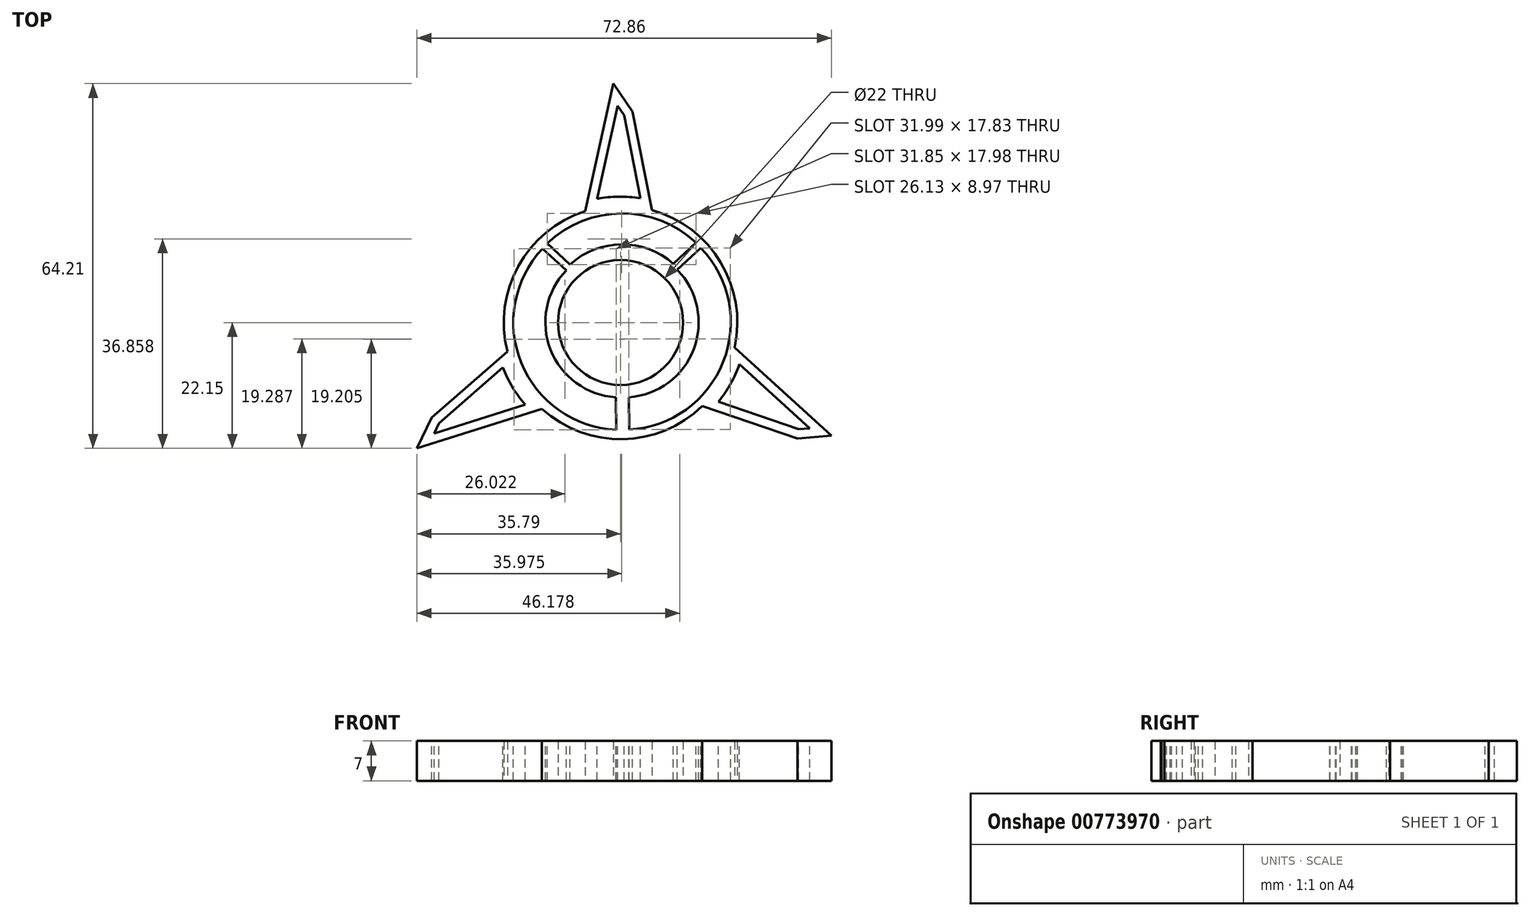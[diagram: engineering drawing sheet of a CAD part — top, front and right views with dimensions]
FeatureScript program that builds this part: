
annotation { "Feature Type Name" : "Feature", "Feature Type Description" : "" }
export const myFeature = defineFeature(function(context is Context, id is Id, definition is map)
    precondition{}
    {
        {
            var Q0;
            Q0=qCreatedBy(makeId("Top.planeOp"),FACE);
            var sketch = newSketch(context, id + "F0", { "sketchPlane" : qUnion([Q0])});
            skCircle(sketch, "E0", {"center": v(0, 0) * mm, "radius": 11 * mm});
            skCircle(sketch, "E1", {"center": v(0, 0) * mm, "radius": 20.54 * mm});
            skLineSegment(sketch, "E2", {"start": v(-6.23, 19.57) * mm, "end": v(0, 47.93) * mm});
            skLineSegment(sketch, "E3", {"start": v(0, 47.93) * mm, "end": v(5.52, 19.79) * mm});
            skLineSegment(sketch, "E4.1.0", {"start": v(-41.5, -23.96) * mm, "end": v(-19.9, -5.11) * mm});
            skLineSegment(sketch, "E4.1.1", {"start": v(-13.83, -15.18) * mm, "end": v(-41.5, -23.96) * mm});
            skLineSegment(sketch, "E4.2.0", {"start": v(41.5, -23.96) * mm, "end": v(14.38, -14.67) * mm});
            skLineSegment(sketch, "E4.2.1", {"start": v(20.07, -4.39) * mm, "end": v(41.5, -23.96) * mm});
            skSolve(sketch);
        }
        {
            var Q0;
            Q0=qSketchRegion(id+"F0",true);
            extrude(context, id + "F1", {"entities" : qUnion([Q0]), "depth" : 7 * mm, "offsetDistance" : 25 * mm});
        }
        {
            var Q0;
            Q0=makeQuery(id+"F1.opExtrude","CAP_FACE",FACE,{"disambiguationData":[OSD([sQuery(id+"F0.wireOp",EDGE,"E0"),sQuery(id+"F0.wireOp",EDGE,"E1"),sQuery(id+"F0.wireOp",EDGE,"E2"),sQuery(id+"F0.wireOp",EDGE,"E3"),sQuery(id+"F0.wireOp",EDGE,"E4.1.0"),sQuery(id+"F0.wireOp",EDGE,"E4.1.1"),sQuery(id+"F0.wireOp",EDGE,"E4.2.0"),sQuery(id+"F0.wireOp",EDGE,"E4.2.1")])],"isStart":false});
            var sketch = newSketch(context, id + "F2", { "sketchPlane" : qUnion([Q0])});
            skLineSegment(sketch, "E5", {"start": v(-13.74, 12.98) * mm, "end": v(-9.55, 9.18) * mm});
            skLineSegment(sketch, "E6", {"start": v(0, 47.93) * mm, "end": v(0.37, -20.54) * mm, "construction": true});
            skLineSegment(sketch, "E7.MirrorCS", {"start": v(14.12, 13.13) * mm, "end": v(9.98, 9.28) * mm});
            skLineSegment(sketch, "E8", {"start": v(-0.8, -13.16) * mm, "end": v(-0.78, -18.87) * mm});
            skLineSegment(sketch, "E9.MirrorCS", {"start": v(1.47, -13.15) * mm, "end": v(1.5, -18.86) * mm});
            skArc(sketch, "E10", {"start": v(-9.55, 9.18) * mm, "mid": v(-12.3, -4.78) * mm, "end": v(-0.8, -13.16) * mm});
            skArc(sketch, "E11", {"start": v(-13.74, 12.98) * mm, "mid": v(-17.46, -7.1) * mm, "end": v(-0.78, -18.87) * mm});
            skLineSegment(sketch, "E12", {"start": v(-12.88, 13.93) * mm, "end": v(-8.89, 10.22) * mm});
            skArc(sketch, "E13.MirrorCS", {"start": v(14.12, 13.13) * mm, "mid": v(18.06, -6.9) * mm, "end": v(1.5, -18.86) * mm});
            skArc(sketch, "E14.MirrorCS", {"start": v(9.98, 9.28) * mm, "mid": v(12.88, -4.65) * mm, "end": v(1.47, -13.15) * mm});
            skLineSegment(sketch, "E15.MirrorCS", {"start": v(13.25, 14.07) * mm, "end": v(9.3, 10.32) * mm});
            skArc(sketch, "E16", {"start": v(9.3, 10.32) * mm, "mid": v(0.19, 13.75) * mm, "end": v(-8.89, 10.22) * mm});
            skArc(sketch, "E17", {"start": v(13.25, 14.07) * mm, "mid": v(0.16, 19.2) * mm, "end": v(-12.88, 13.93) * mm});
            skSolve(sketch);
        }
        {
            var Q0;
            Q0=qSketchRegion(id+"F2",true);
            extrude(context, id + "F3", {"entities" : qUnion([Q0]), "operationType" : NewBodyOperationType.REMOVE, "oppositeDirection" : true, "depth" : 25 * mm, "offsetDistance" : 25 * mm});
        }
        {
            var Q0;
            Q0=makeQuery(id+"F1.opExtrude","SWEPT_EDGE",EDGE,{"disambiguationData":[OSD([sQuery(id+"F0.wireOp",EDGE,"E4.1.0"),sQuery(id+"F0.wireOp",EDGE,"E4.1.1")])]});
            var Q1;
            Q1=makeQuery(id+"F1.opExtrude","SWEPT_EDGE",EDGE,{"disambiguationData":[OSD([sQuery(id+"F0.wireOp",EDGE,"E2"),sQuery(id+"F0.wireOp",EDGE,"E3")])]});
            var Q2;
            Q2=makeQuery(id+"F1.opExtrude","SWEPT_EDGE",EDGE,{"disambiguationData":[OSD([sQuery(id+"F0.wireOp",EDGE,"E4.2.0"),sQuery(id+"F0.wireOp",EDGE,"E4.2.1")])]});
            chamfer(context, id + "F4", {"entities" : qUnion([Q0, Q1, Q2]), "chamferType" : ChamferType.TWO_OFFSETS, "width1" : 6 * mm, "oppositeDirection" : false, "width2" : 11 * mm, "tangentPropagation" : true});
        }
        {
            var Q0;
            Q0=makeQuery(id+"F1.opExtrude","CAP_FACE",FACE,{"disambiguationData":[OSD([sQuery(id+"F0.wireOp",EDGE,"E0"),sQuery(id+"F0.wireOp",EDGE,"E1"),sQuery(id+"F0.wireOp",EDGE,"E2"),sQuery(id+"F0.wireOp",EDGE,"E3"),sQuery(id+"F0.wireOp",EDGE,"E4.1.0"),sQuery(id+"F0.wireOp",EDGE,"E4.1.1"),sQuery(id+"F0.wireOp",EDGE,"E4.2.0"),sQuery(id+"F0.wireOp",EDGE,"E4.2.1")])],"isStart":false});
            var sketch = newSketch(context, id + "F5", { "sketchPlane" : qUnion([Q0])});
            skArc(sketch, "E18", {"start": v(5.52, 19.79) * mm, "mid": v(-0.37, 20.55) * mm, "end": v(-6.23, 19.57) * mm});
            skArc(sketch, "E19.0", {"start": v(3.48, 21.87) * mm, "mid": v(-0.32, 22.15) * mm, "end": v(-4.11, 21.76) * mm});
            skLineSegment(sketch, "E19.1", {"start": v(0.61, 36.5) * mm, "end": v(3.48, 21.87) * mm});
            skLineSegment(sketch, "E19.2", {"start": v(0.61, 36.5) * mm, "end": v(-0.52, 38.13) * mm});
            skLineSegment(sketch, "E19.3", {"start": v(-4.11, 21.76) * mm, "end": v(-0.52, 38.13) * mm});
            skLineSegment(sketch, "E20.1.0", {"start": v(-31.91, -17.72) * mm, "end": v(-20.68, -7.92) * mm});
            skLineSegment(sketch, "E20.1.1", {"start": v(-31.91, -17.72) * mm, "end": v(-32.76, -19.51) * mm});
            skLineSegment(sketch, "E20.1.2", {"start": v(-16.79, -14.44) * mm, "end": v(-32.76, -19.51) * mm});
            skArc(sketch, "E20.1.3", {"start": v(-20.68, -7.92) * mm, "mid": v(-19.02, -11.35) * mm, "end": v(-16.79, -14.44) * mm});
            skLineSegment(sketch, "E20.2.0", {"start": v(31.3, -18.78) * mm, "end": v(17.2, -13.95) * mm});
            skLineSegment(sketch, "E20.2.1", {"start": v(31.3, -18.78) * mm, "end": v(33.28, -18.62) * mm});
            skLineSegment(sketch, "E20.2.2", {"start": v(20.9, -7.32) * mm, "end": v(33.28, -18.62) * mm});
            skArc(sketch, "E20.2.3", {"start": v(17.2, -13.95) * mm, "mid": v(19.34, -10.8) * mm, "end": v(20.9, -7.32) * mm});
            skPoint(sketch, "E20.center", {"position": v(0, 0) * mm});
            skSolve(sketch);
        }
        {
            var Q0;
            Q0=qSketchRegion(id+"F5",true);
            extrude(context, id + "F6", {"entities" : qUnion([Q0]), "operationType" : NewBodyOperationType.REMOVE, "oppositeDirection" : true, "depth" : 25 * mm, "offsetDistance" : 25 * mm});
        }
    });
